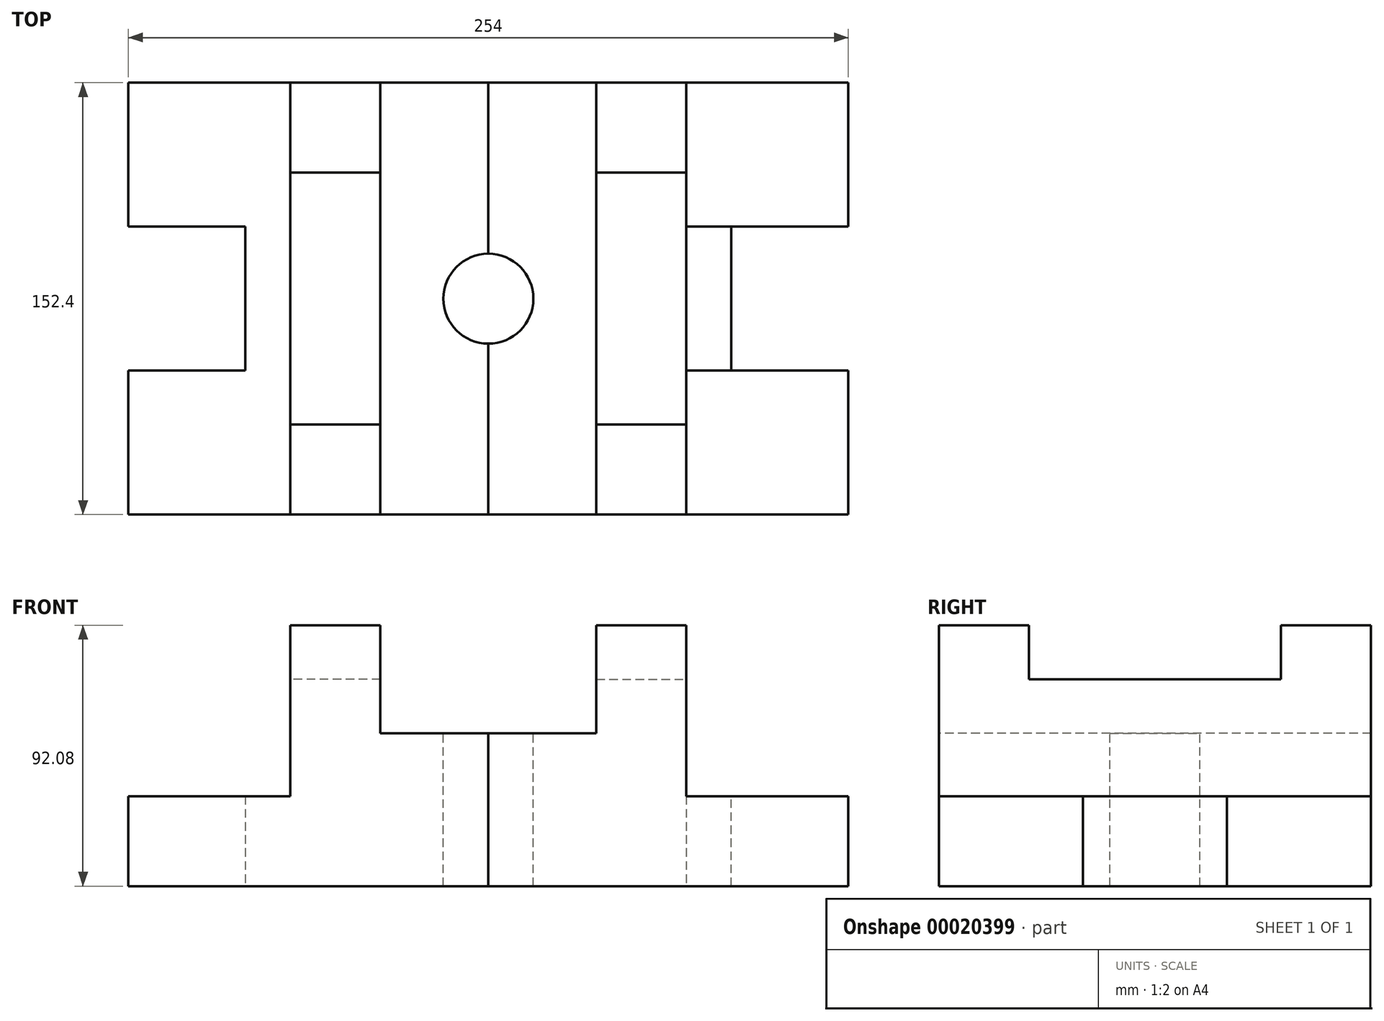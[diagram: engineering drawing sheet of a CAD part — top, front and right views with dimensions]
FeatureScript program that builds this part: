
annotation { "Feature Type Name" : "Feature", "Feature Type Description" : "" }
export const myFeature = defineFeature(function(context is Context, id is Id, definition is map)
    precondition{}
    {
        {
            var Q0;
            Q0=qCreatedBy(makeId("Front.planeOp"),FACE);
            var sketch = newSketch(context, id + "F0", { "sketchPlane" : qUnion([Q0])});
            skLineSegment(sketch, "E0", {"start": v(52.99, -62.99) * mm, "end": v(52.99, -31.24) * mm});
            skLineSegment(sketch, "E1", {"start": v(52.99, -31.24) * mm, "end": v(-4.16, -31.24) * mm});
            skLineSegment(sketch, "E2", {"start": v(-4.16, -31.24) * mm, "end": v(-4.16, 29.09) * mm});
            skLineSegment(sketch, "E3", {"start": v(-4.16, 29.09) * mm, "end": v(-35.91, 29.09) * mm});
            skLineSegment(sketch, "E4", {"start": v(-35.91, 29.09) * mm, "end": v(-35.91, -9.01) * mm});
            skLineSegment(sketch, "E5", {"start": v(-35.91, -9.01) * mm, "end": v(-74.01, -9.01) * mm});
            skLineSegment(sketch, "E6", {"start": v(-74.01, -9.01) * mm, "end": v(-74.01, -62.99) * mm});
            skLineSegment(sketch, "E7", {"start": v(-74.01, -62.99) * mm, "end": v(52.99, -62.99) * mm});
            skLineSegment(sketch, "E8", {"start": v(-35.91, 10.04) * mm, "end": v(-4.16, 10.04) * mm});
            skSolve(sketch);
        }
        {
            var Q0;
            Q0=makeQuery(id+"F0.imprint","IMPRINT",FACE,{"disambiguationData":[TD([[makeQuery(id+"F0.imprint","IMPRINT",EDGE,{"derivedFrom":sQuery(id+"F0.wireOp",EDGE,"E0")}),1.0]])]});
            extrude(context, id + "F1", {"entities" : qUnion([Q0]), "depth" : 50.8 * mm});
        }
        {
            var Q0;
            Q0=makeQuery(id+"F0.imprint","IMPRINT",FACE,{"disambiguationData":[TD([[makeQuery(id+"F0.imprint","IMPRINT",EDGE,{"derivedFrom":sQuery(id+"F0.wireOp",EDGE,"E0")}),1.0]])]});
            var sketch = newSketch(context, id + "F2", { "sketchPlane" : qUnion([Q0])});
            skLineSegment(sketch, "E9", {"start": v(11.71, -62.99) * mm, "end": v(52.99, -62.99) * mm});
            skLineSegment(sketch, "E10", {"start": v(52.99, -62.99) * mm, "end": v(52.99, -16.23) * mm});
            skLineSegment(sketch, "E11", {"start": v(11.71, -16.23) * mm, "end": v(52.99, -16.23) * mm});
            skLineSegment(sketch, "E12", {"start": v(-4.16, -31.28) * mm, "end": v(-4.16, -62.99) * mm});
            skLineSegment(sketch, "E13", {"start": v(-4.16, -31.28) * mm, "end": v(-4.16, -10.02) * mm});
            skLineSegment(sketch, "E14", {"start": v(11.71, -16.23) * mm, "end": v(11.71, -10.02) * mm});
            skLineSegment(sketch, "E15", {"start": v(-4.16, -10.02) * mm, "end": v(11.71, -10.02) * mm});
            skLineSegment(sketch, "E16", {"start": v(-4.16, -62.99) * mm, "end": v(-74.01, -62.99) * mm});
            skLineSegment(sketch, "E17", {"start": v(-74.01, -62.99) * mm, "end": v(-74.01, -9.01) * mm});
            skLineSegment(sketch, "E18", {"start": v(-74.01, -9.01) * mm, "end": v(-35.91, -9.01) * mm});
            skLineSegment(sketch, "E19", {"start": v(-35.91, -9.01) * mm, "end": v(-35.91, 29.09) * mm});
            skLineSegment(sketch, "E20", {"start": v(-35.91, 10.04) * mm, "end": v(-4.16, 10.04) * mm});
            skLineSegment(sketch, "E21", {"start": v(-4.16, 10.04) * mm, "end": v(-4.16, -10.02) * mm});
            skLineSegment(sketch, "E22", {"start": v(-4.16, -10.02) * mm, "end": v(-4.16, 10.04) * mm});
            skSolve(sketch);
        }
        {
            var Q0;
            Q0=makeQuery(id+"F1.opExtrude","CAP_FACE",FACE,{"disambiguationData":[OSD([sQuery(id+"F0.wireOp",EDGE,"E0"),sQuery(id+"F0.wireOp",EDGE,"E1"),sQuery(id+"F0.wireOp",EDGE,"E2"),sQuery(id+"F0.wireOp",EDGE,"E4"),sQuery(id+"F0.wireOp",EDGE,"E5"),sQuery(id+"F0.wireOp",EDGE,"E6"),sQuery(id+"F0.wireOp",EDGE,"E7"),sQuery(id+"F0.wireOp",EDGE,"E8")])],"isStart":false});
            var sketch = newSketch(context, id + "F3", { "sketchPlane" : qUnion([Q0])});
            skLineSegment(sketch, "E23", {"start": v(-4.16, 10.04) * mm, "end": v(-4.16, 29.09) * mm});
            skLineSegment(sketch, "E24", {"start": v(-4.16, 29.09) * mm, "end": v(-35.91, 29.09) * mm});
            skLineSegment(sketch, "E25", {"start": v(-35.91, 10.04) * mm, "end": v(-35.91, 29.09) * mm});
            skSolve(sketch);
        }
        {
            var Q0;
            Q0=makeQuery(id+"F3.imprint","IMPRINT",FACE,{"disambiguationData":[TD([[makeQuery(id+"F3.imprint","IMPRINT",EDGE,{"derivedFrom":sQuery(id+"F3.wireOp",EDGE,"E23")}),1.0]])]});
            extrude(context, id + "F4", {"entities" : qUnion([Q0]), "oppositeDirection" : true, "depth" : 31.75 * mm});
        }
        {
            var Q0;
            {var subQ5=sQuery(id+"F2.wireOp",EDGE,"E12");Q0=makeQuery(id+"F2.imprint","IMPRINT",FACE,{"disambiguationData":[TD([[makeQuery(id+"F2.imprint","IMPRINT",EDGE,{"derivedFrom":subQ5}),-1.0]])]});}
            extrude(context, id + "F5", {"entities" : qUnion([Q0]), "oppositeDirection" : true, "depth" : 25.4 * mm});
        }
        {
            var Q0;
            Q0=makeQuery(id+"F5.opExtrude","SWEPT_FACE",FACE,{"disambiguationData":[OSD([sQuery(id+"F2.wireOp",EDGE,"E18")])]});
            var sketch = newSketch(context, id + "F6", { "sketchPlane" : qUnion([Q0])});
            skCircle(sketch, "E26", {"center": v(-74.01, 25.4) * mm, "radius": 15.88 * mm});
            skLineSegment(sketch, "E27", {"start": v(-58.14, 25.4) * mm, "end": v(-74.01, 25.4) * mm});
            skLineSegment(sketch, "E28", {"start": v(-74.01, 25.4) * mm, "end": v(-74.01, 9.53) * mm});
            skSolve(sketch);
        }
        {
            var Q0;
            {var subQ1=sQuery(id+"F6.wireOp",EDGE,"E27");Q0=makeQuery(id+"F6.imprint","IMPRINT",FACE,{"disambiguationData":[TD([[makeQuery(id+"F6.imprint","IMPRINT",EDGE,{"derivedFrom":subQ1}),1.0]])]});}
            extrude(context, id + "F7", {"entities" : qUnion([Q0]), "operationType" : NewBodyOperationType.REMOVE, "endBound" : BoundingType.THROUGH_ALL, "oppositeDirection" : true, "depth" : 25.4 * mm});
        }
        {
            var Q0;
            Q0=makeQuery(id+"F5.opExtrude","SWEPT_BODY",BODY,{"disambiguationData":[OSD([sQuery(id+"F2.wireOp",EDGE,"E12"),sQuery(id+"F2.wireOp",EDGE,"E13"),sQuery(id+"F2.wireOp",EDGE,"E16"),sQuery(id+"F2.wireOp",EDGE,"E17"),sQuery(id+"F2.wireOp",EDGE,"E18"),sQuery(id+"F2.wireOp",EDGE,"E19"),sQuery(id+"F2.wireOp",EDGE,"E20"),sQuery(id+"F2.wireOp",EDGE,"E22")])]});
            var Q1;
            Q1=makeQuery(id+"F1.opExtrude","SWEPT_BODY",BODY,{"disambiguationData":[OSD([sQuery(id+"F0.wireOp",EDGE,"E0"),sQuery(id+"F0.wireOp",EDGE,"E1"),sQuery(id+"F0.wireOp",EDGE,"E2"),sQuery(id+"F0.wireOp",EDGE,"E4"),sQuery(id+"F0.wireOp",EDGE,"E5"),sQuery(id+"F0.wireOp",EDGE,"E6"),sQuery(id+"F0.wireOp",EDGE,"E7"),sQuery(id+"F0.wireOp",EDGE,"E8")])]});
            var Q2;
            Q2=makeQuery(id+"F4.opExtrude","SWEPT_BODY",BODY,{"disambiguationData":[OSD([sQuery(id+"F0.wireOp",EDGE,"E8"),sQuery(id+"F3.wireOp",EDGE,"E23"),sQuery(id+"F3.wireOp",EDGE,"E24"),sQuery(id+"F3.wireOp",EDGE,"E25")])]});
            var Q3;
            Q3=makeQuery(id+"F5.opExtrude","CAP_FACE",FACE,{"disambiguationData":[OSD([sQuery(id+"F2.wireOp",EDGE,"E12"),sQuery(id+"F2.wireOp",EDGE,"E13"),sQuery(id+"F2.wireOp",EDGE,"E16"),sQuery(id+"F2.wireOp",EDGE,"E17"),sQuery(id+"F2.wireOp",EDGE,"E18"),sQuery(id+"F2.wireOp",EDGE,"E19"),sQuery(id+"F2.wireOp",EDGE,"E20"),sQuery(id+"F2.wireOp",EDGE,"E22")])],"isStart":false});
            mirror(context, id + "F8", {"operationType" : NewBodyOperationType.ADD, "entities" : qUnion([Q0, Q1, Q2]), "mirrorPlane" : qUnion([Q3])});
        }
        {
            var Q0;
            Q0=makeQuery(id+"F5.opExtrude","SWEPT_BODY",BODY,{"disambiguationData":[OSD([sQuery(id+"F2.wireOp",EDGE,"E12"),sQuery(id+"F2.wireOp",EDGE,"E13"),sQuery(id+"F2.wireOp",EDGE,"E16"),sQuery(id+"F2.wireOp",EDGE,"E17"),sQuery(id+"F2.wireOp",EDGE,"E18"),sQuery(id+"F2.wireOp",EDGE,"E19"),sQuery(id+"F2.wireOp",EDGE,"E20"),sQuery(id+"F2.wireOp",EDGE,"E22")])]});
            var Q1;
            Q1=makeQuery(id+"F1.opExtrude","SWEPT_BODY",BODY,{"disambiguationData":[OSD([sQuery(id+"F0.wireOp",EDGE,"E0"),sQuery(id+"F0.wireOp",EDGE,"E1"),sQuery(id+"F0.wireOp",EDGE,"E2"),sQuery(id+"F0.wireOp",EDGE,"E4"),sQuery(id+"F0.wireOp",EDGE,"E5"),sQuery(id+"F0.wireOp",EDGE,"E6"),sQuery(id+"F0.wireOp",EDGE,"E7"),sQuery(id+"F0.wireOp",EDGE,"E8")])]});
            var Q2;
            Q2=makeQuery(id+"F4.opExtrude","SWEPT_BODY",BODY,{"disambiguationData":[OSD([sQuery(id+"F0.wireOp",EDGE,"E8"),sQuery(id+"F3.wireOp",EDGE,"E23"),sQuery(id+"F3.wireOp",EDGE,"E24"),sQuery(id+"F3.wireOp",EDGE,"E25")])]});
            var Q3;
            Q3=makeQuery(id+"F8.boolean.opBoolean","MERGE",FACE,{"derivedFrom":[makeQuery(id+"F8.opPattern","COPY",FACE,{"derivedFrom":makeQuery(id+"F1.opExtrude","SWEPT_FACE",FACE,{"disambiguationData":[OSD([sQuery(id+"F0.wireOp",EDGE,"E6")])]}),"instanceName":"1"}),makeQuery(id+"F8.opPattern","COPY",FACE,{"derivedFrom":makeQuery(id+"F5.opExtrude","SWEPT_FACE",FACE,{"disambiguationData":[OSD([sQuery(id+"F2.wireOp",EDGE,"E17")])]}),"instanceName":"1"})]});
            mirror(context, id + "F9", {"entities" : qUnion([Q0, Q1, Q2]), "mirrorPlane" : qUnion([Q3])});
        }
        {
            var Q0;
            Q0=makeQuery(id+"F1.opExtrude","CAP_FACE",FACE,{"disambiguationData":[OSD([sQuery(id+"F0.wireOp",EDGE,"E0"),sQuery(id+"F0.wireOp",EDGE,"E1"),sQuery(id+"F0.wireOp",EDGE,"E2"),sQuery(id+"F0.wireOp",EDGE,"E4"),sQuery(id+"F0.wireOp",EDGE,"E5"),sQuery(id+"F0.wireOp",EDGE,"E6"),sQuery(id+"F0.wireOp",EDGE,"E7"),sQuery(id+"F0.wireOp",EDGE,"E8")])],"isStart":true});
            var sketch = newSketch(context, id + "F10", { "sketchPlane" : qUnion([Q0])});
            skLineSegment(sketch, "E29", {"start": v(-11.71, -62.99) * mm, "end": v(-11.71, -31.24) * mm});
            skLineSegment(sketch, "E30", {"start": v(4.16, -31.24) * mm, "end": v(4.16, -62.99) * mm});
            skLineSegment(sketch, "E31", {"start": v(4.16, -31.24) * mm, "end": v(-11.71, -31.24) * mm});
            skLineSegment(sketch, "E32", {"start": v(4.16, -62.99) * mm, "end": v(-11.71, -62.99) * mm});
            skSolve(sketch);
        }
        {
            var Q0;
            Q0=makeQuery(id+"F10.imprint","IMPRINT",FACE,{"disambiguationData":[TD([[makeQuery(id+"F10.imprint","IMPRINT",EDGE,{"derivedFrom":sQuery(id+"F10.wireOp",EDGE,"E29")}),-1.0]])]});
            extrude(context, id + "F11", {"entities" : qUnion([Q0]), "depth" : 50.8 * mm});
        }
        {
            var Q0;
            Q0=makeQuery(id+"F9.opPattern","COPY",FACE,{"derivedFrom":makeQuery(id+"F8.opPattern","COPY",FACE,{"derivedFrom":makeQuery(id+"F1.opExtrude","CAP_FACE",FACE,{"disambiguationData":[OSD([sQuery(id+"F0.wireOp",EDGE,"E0"),sQuery(id+"F0.wireOp",EDGE,"E1"),sQuery(id+"F0.wireOp",EDGE,"E2"),sQuery(id+"F0.wireOp",EDGE,"E4"),sQuery(id+"F0.wireOp",EDGE,"E5"),sQuery(id+"F0.wireOp",EDGE,"E6"),sQuery(id+"F0.wireOp",EDGE,"E7"),sQuery(id+"F0.wireOp",EDGE,"E8")])],"isStart":true}),"instanceName":"1"}),"instanceName":"1"});
            var sketch = newSketch(context, id + "F12", { "sketchPlane" : qUnion([Q0])});
            skLineSegment(sketch, "E33", {"start": v(-159.74, -31.24) * mm, "end": v(-159.74, -62.99) * mm});
            skLineSegment(sketch, "E34", {"start": v(-143.86, -31.24) * mm, "end": v(-143.86, -62.99) * mm});
            skLineSegment(sketch, "E35", {"start": v(-143.86, -31.24) * mm, "end": v(-159.74, -31.24) * mm});
            skLineSegment(sketch, "E36", {"start": v(-143.86, -62.99) * mm, "end": v(-159.74, -62.99) * mm});
            skSolve(sketch);
        }
        {
            var Q0;
            Q0=makeQuery(id+"F12.imprint","IMPRINT",FACE,{"disambiguationData":[TD([[makeQuery(id+"F12.imprint","IMPRINT",EDGE,{"derivedFrom":sQuery(id+"F12.wireOp",EDGE,"E33")}),1.0]])]});
            extrude(context, id + "F13", {"entities" : qUnion([Q0]), "operationType" : NewBodyOperationType.ADD, "depth" : 50.8 * mm});
        }
    });
